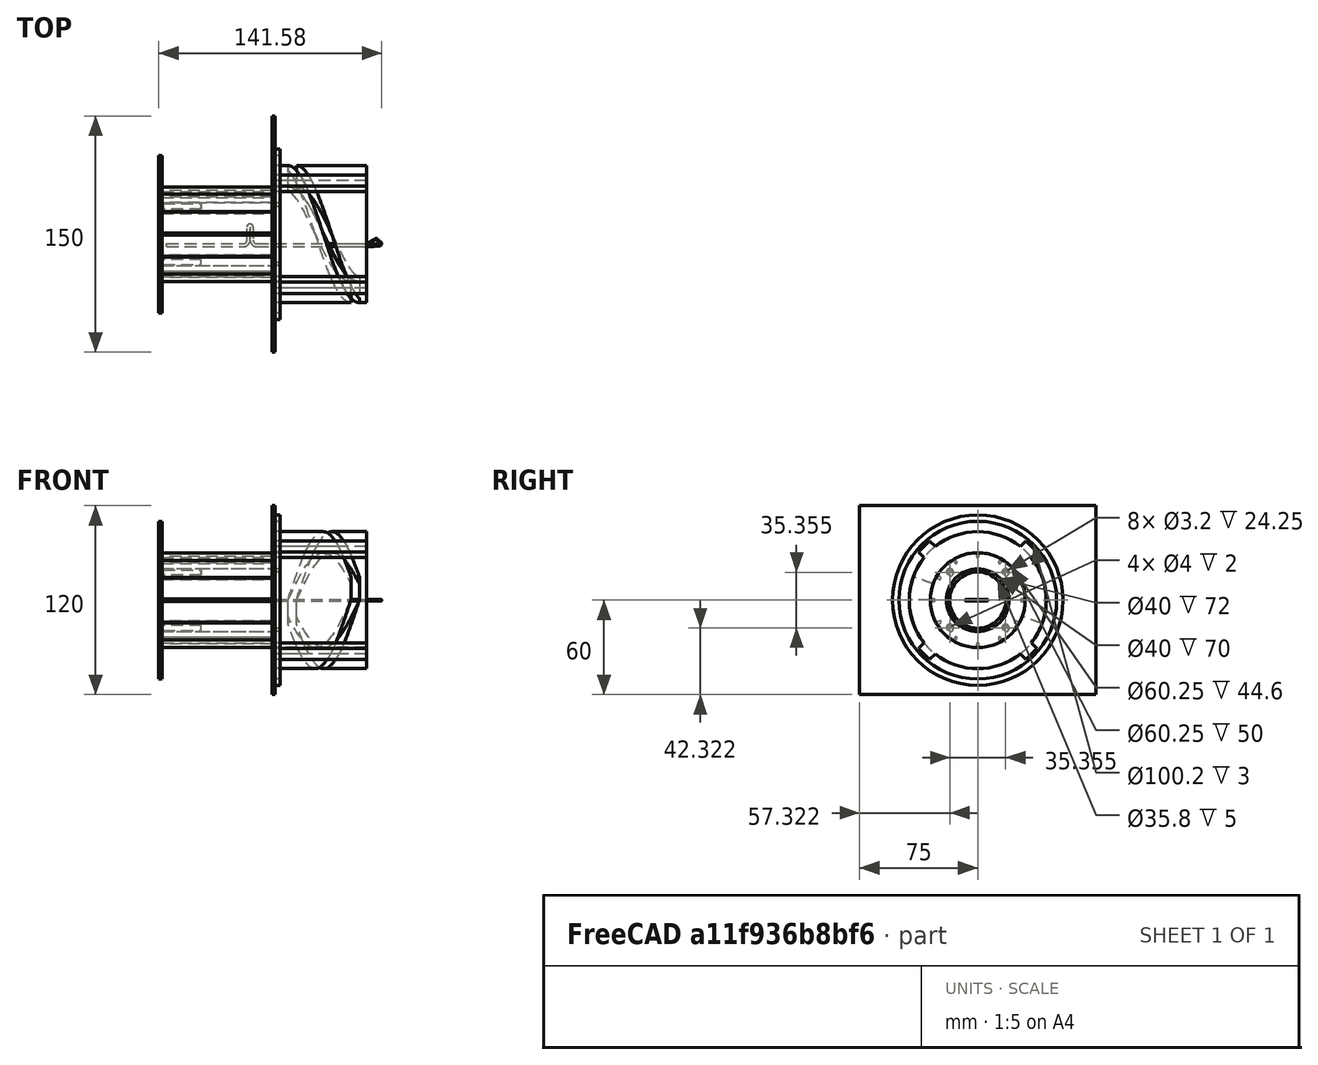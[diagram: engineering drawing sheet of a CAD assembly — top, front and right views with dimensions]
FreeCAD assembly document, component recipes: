
FREECAD ASSEMBLY — COMPONENT RECIPES ("knitting_machine")

This assembly document has 5 components, labeled P0..P4 below (a component is one placed body or linked part). 5 of them carry a construction recipe — the FreeCAD feature program that regenerates the part from scratch, quoted from this document or its linked companion documents; the rest are supplied as boundary geometry only. No exploded tour is included for this assembly.
COMPONENT P0 — recipe-attached ("Baseplate001", modeled in this document).
Construction recipe (the document's own serialized feature program — sketch geometry with constraints, then the solid features built on it; lengths are millimeters unless a unit is written):

FEATURE [Sketcher::SketchObject] Sketch012
  ArcFitTolerance = 1e-06
  AttachmentSupport = -> [YZ_Plane005]
  FullyConstrained = true
  MakeInternals = false
  MapMode = 5
  Placement = pos=(0,0,0) rot=(0.57735,0.57735,0.57735;2.0944rad)
  expr: Constraints[13] = <<MasterSpreadsheet>>.hole_diameter - 0.2 mm
  sketch-geometry (6):
    g0: LineSegment StartX=-75 StartY=60 StartZ=0 EndX=-75 EndY=-60 EndZ=0
    g1: LineSegment StartX=-75 StartY=-60 StartZ=0 EndX=75 EndY=-60 EndZ=0
    g2: LineSegment StartX=75 StartY=-60 StartZ=0 EndX=75 EndY=60 EndZ=0
    g3: LineSegment StartX=75 StartY=60 StartZ=0 EndX=-75 EndY=60 EndZ=0
    g4: GeomPoint [constr] X=0 Y=0 Z=0
    g5: Circle CenterX=0 CenterY=0 CenterZ=0 NormalX=0 NormalY=0 NormalZ=1 AngleXU=0 Radius=19.9
  constraints (14):
    c: Coincident(g0,g1)
    c: Coincident(g1,g2)
    c: Coincident(g2,g3)
    c: Coincident(g3,g0)
    c: Vertical(g0)
    c: Vertical(g2)
    c: Horizontal(g1)
    c: Horizontal(g3)
    c: Symmetric(g2,g0,g4)
    c: Coincident(g4,g-1)
    c: Coincident(g5,g4)
    c: DistanceX(g1,g1) = 150
    c: DistanceY(g0,g0) = 120
    c: Diameter(g5) = 39.8
FEATURE [PartDesign::Pad] Pad004
  Direction = (1,0,0)
  Length = 2
  Length2 = 10
  Placement = pos=(0,0,0) rot=(1,1,1;2.0944rad)
  Profile = -> Sketch012
  ReferenceAxis = -> Sketch012 [N_Axis]
  Refine = true
  Suppressed = false
  Type = 0
FEATURE [Sketcher::SketchObject] Sketch013
  ArcFitTolerance = 1e-06
  AttachmentSupport = -> [YZ_Plane005]
  ExternalGeometry = -> [Pad004]
  FullyConstrained = true
  MakeInternals = false
  MapMode = 5
  Placement = pos=(0,0,0) rot=(0.57735,0.57735,0.57735;2.0944rad)
  sketch-geometry (2):
    g0: Circle CenterX=0 CenterY=0 CenterZ=0 NormalX=0 NormalY=0 NormalZ=1 AngleXU=0 Radius=19.9
    g1: Circle CenterX=0 CenterY=0 CenterZ=0 NormalX=0 NormalY=0 NormalZ=1 AngleXU=0 Radius=17.9
  constraints (4):
    c: Coincident(g0,g-1)
    c: Equal(g-3,g0)
    c: Coincident(g1,g0)
    c: Distance(g1,g0) = 2
FEATURE [PartDesign::Pad] Pad005
  BaseFeature = -> Pad004
  Direction = (1,0,0)
  Length = 5
  Length2 = 10
  Offset = 1
  Placement = pos=(0,0,0) rot=(1,1,1;2.0944rad)
  Profile = -> Sketch013
  ReferenceAxis = -> Sketch013 [N_Axis]
  Refine = true
  Suppressed = false
  Type = 0
FEATURE [Sketcher::SketchObject] Sketch014
  ArcFitTolerance = 1e-06
  AttachmentSupport = -> [YZ_Plane005]
  FullyConstrained = true
  MakeInternals = false
  MapMode = 5
  Placement = pos=(0,0,0) rot=(0.57735,0.57735,0.57735;2.0944rad)
  sketch-geometry (2):
    g0: Circle CenterX=0 CenterY=0 CenterZ=0 NormalX=0 NormalY=0 NormalZ=1 AngleXU=0 Radius=50.1
    g1: Circle CenterX=0 CenterY=0 CenterZ=0 NormalX=0 NormalY=0 NormalZ=1 AngleXU=0 Radius=54.1
  constraints (4):
    c: Coincident(g0,g-1)
    c: Coincident(g1,g0)
    c: Diameter(g0) = 100.2
    c: Distance(g0,g1) = 4
FEATURE [PartDesign::Pad] Pad006
  BaseFeature = -> Pad005
  Direction = (1,0,0)
  Length = 10
  Length2 = 10
  Placement = pos=(0,0,0) rot=(1,1,1;2.0944rad)
  Profile = -> Sketch014
  ReferenceAxis = -> Sketch014 [N_Axis]
  Refine = true
  Suppressed = false
  Type = 3
  UpToFace = -> Pad005 [Face7]
FEATURE [PartDesign::Body] Body002  label="Body_baseplate"
  AllowCompound = false
  Group = -> [Sketch012,Pad004,Sketch013,Pad005,Sketch014,Pad006]
  Origin = -> Origin005
  Tip = -> Pad006
COMPONENT P1 — recipe-attached ("Needle001", modeled in this document).
Construction recipe (the document's own serialized feature program — sketch geometry with constraints, then the solid features built on it; lengths are millimeters unless a unit is written):

FEATURE [Sketcher::SketchObject] Sketch  label="Needle_profile"
  ArcFitTolerance = 1e-06
  AttachmentSupport = -> [XY_Plane001]
  FullyConstrained = true
  MakeInternals = false
  MapMode = 5
  expr: Constraints[19] = <<MasterSpreadsheet>>.needle_thickness + 0.1 mm
  expr: Constraints[29] = <<MasterSpreadsheet>>.needle_knob_protrusion
  sketch-geometry (11):
    g0: LineSegment StartX=-67 StartY=-7 StartZ=0 EndX=-18.2 EndY=-7 EndZ=0
    g1: LineSegment StartX=-15 StartY=-3.8 StartZ=0 EndX=-15 EndY=4.55 EndZ=0
    g2: LineSegment StartX=-13.95 StartY=5.5 StartZ=0 EndX=-14.05 EndY=5.5 EndZ=0
    g3: LineSegment StartX=-13 StartY=4.55 StartZ=0 EndX=-13 EndY=-3.8 EndZ=0
    g4: LineSegment StartX=-9.8 StartY=-7 StartZ=0 EndX=60 EndY=-7 EndZ=0
    g5: ArcOfCircle CenterX=-18.2 CenterY=-3.8 CenterZ=0 NormalX=0 NormalY=0 NormalZ=1 AngleXU=0 Radius=3.2 StartAngle=4.71239 EndAngle=6.28319
    g6: GeomPoint [constr] X=-15 Y=-7 Z=0
    g7: ArcOfCircle CenterX=-9.8 CenterY=-3.8 CenterZ=0 NormalX=0 NormalY=0 NormalZ=1 AngleXU=0 Radius=3.2 StartAngle=3.14159 EndAngle=4.71239
    g8: GeomPoint [constr] X=-13 Y=-7 Z=0
    g9: ArcOfCircle CenterX=-14.05 CenterY=4.55 CenterZ=0 NormalX=0 NormalY=0 NormalZ=1 AngleXU=0 Radius=0.95 StartAngle=1.5708 EndAngle=3.14159
    g10: ArcOfCircle CenterX=-13.95 CenterY=4.55 CenterZ=0 NormalX=0 NormalY=0 NormalZ=1 AngleXU=0 Radius=0.95 StartAngle=3e-16 EndAngle=1.5708
  constraints (30):
    c: Horizontal(g0)
    c: Vertical(g1)
    c: Vertical(g3)
    c: Horizontal(g4)
    c: Horizontal(g8,g6)
    c: Horizontal(g2)
    c: PointOnObject(g6,g0)
    c: PointOnObject(g6,g1)
    c: Tangent(g0,g5) = -1.5708
    c: Tangent(g1,g5) = -1.5708
    c: PointOnObject(g8,g3)
    c: PointOnObject(g8,g4)
    c: Tangent(g3,g7) = -1.5708
    c: Tangent(g4,g7) = -1.5708
    c: Equal(g5,g7)
    c: Distance(g0,g-1) = 7
    c: Distance(g0,g-2) = 67
    c: DistanceX(g-1,g4) = 60
    c: Distance(g3,g-2) = 13
    c: DistanceX(g1,g3) = 2
    c: Horizontal(g1,g3)
    c: Radius(g7) = 3.2
    c: Distance(g2,g2) = 0.1
    c: Coincident(g9,g1)
    c: Horizontal(g9,g1)
    c: Tangent(g9,g2) = -1.5708
    c: Coincident(g10,g3)
    c: Horizontal(g10,g3)
    c: Tangent(g10,g2) = -1.5708
    c: DistanceY(g4,g2) = 12.5
FEATURE [Sketcher::SketchObject] Sketch001  label="Needle_section"
  ArcFitTolerance = 1e-06
  AttachmentSupport = -> [YZ_Plane001]
  ExternalGeometry = -> [Sketch]
  FullyConstrained = true
  MakeInternals = false
  MapMode = 5
  Placement = pos=(0,0,0) rot=(0.57735,0.57735,0.57735;2.0944rad)
  expr: Constraints[26] = <<MasterSpreadsheet>>.needle_thickness
  expr: Constraints[27] = <<MasterSpreadsheet>>.needle_width
  sketch-geometry (13):
    g0: LineSegment StartX=-7.95 StartY=0.1 StartZ=0 EndX=-7.95 EndY=-0.1 EndZ=0
    g1: LineSegment StartX=-7.45 StartY=-0.6 StartZ=0 EndX=-6.55 EndY=-0.6 EndZ=0
    g2: LineSegment StartX=-6.05 StartY=-0.1 StartZ=0 EndX=-6.05 EndY=0.1 EndZ=0
    g3: LineSegment StartX=-6.55 StartY=0.6 StartZ=0 EndX=-7.45 EndY=0.6 EndZ=0
    g4: ArcOfCircle CenterX=-7.45 CenterY=0.1 CenterZ=0 NormalX=0 NormalY=0 NormalZ=1 AngleXU=0 Radius=0.5 StartAngle=1.5708 EndAngle=3.14159
    g5: ArcOfCircle CenterX=-7.45 CenterY=-0.1 CenterZ=0 NormalX=0 NormalY=0 NormalZ=1 AngleXU=0 Radius=0.5 StartAngle=3.14159 EndAngle=4.71239
    g6: ArcOfCircle CenterX=-6.55 CenterY=-0.1 CenterZ=0 NormalX=0 NormalY=0 NormalZ=1 AngleXU=0 Radius=0.5 StartAngle=4.71239 EndAngle=6.28319
    g7: ArcOfCircle CenterX=-6.55 CenterY=0.1 CenterZ=0 NormalX=0 NormalY=0 NormalZ=1 AngleXU=0 Radius=0.5 StartAngle=0 EndAngle=1.5708
    g8: GeomPoint [constr] X=-7.95 Y=0.6 Z=0
    g9: GeomPoint [constr] X=-6.05 Y=-0.6 Z=0
    g10: LineSegment [constr] StartX=-7.45 StartY=-0.1 StartZ=0 EndX=-6.55 EndY=0.1 EndZ=0
    g11: LineSegment [constr] StartX=-7.45 StartY=0.1 StartZ=0 EndX=-6.55 EndY=-0.1 EndZ=0
    g12: GeomPoint [constr] X=-7 Y=0 Z=0
  constraints (28):
    c: Tangent(g0,g4) = -1.5708
    c: Tangent(g0,g5) = -1.5708
    c: Tangent(g1,g5) = -1.5708
    c: Tangent(g1,g6) = -1.5708
    c: Tangent(g2,g6) = -1.5708
    c: Tangent(g2,g7) = -1.5708
    c: Tangent(g3,g7) = -1.5708
    c: Tangent(g3,g4) = -1.5708
    c: Vertical(g0)
    c: Vertical(g2)
    c: Horizontal(g1)
    c: Horizontal(g3)
    c: Equal(g4,g5)
    c: Equal(g5,g6)
    c: Equal(g6,g7)
    c: PointOnObject(g8,g0)
    c: PointOnObject(g8,g3)
    c: PointOnObject(g9,g1)
    c: PointOnObject(g9,g2)
    c: Radius(g5) = 0.5
    c: Coincident(g10,g5)
    c: Coincident(g10,g7)
    c: Coincident(g11,g4)
    c: Coincident(g11,g6)
    c: Symmetric(g10,g10,g12)
    c: Coincident(g12,g-3)
    c: DistanceX(g0,g2) = 1.9
    c: DistanceY(g1,g3) = 1.2
FEATURE [PartDesign::AdditivePipe] AdditivePipe
  AuxilleryCurvelinear = true
  AuxillerySpineTangent = false
  Binormal = (0,0,0)
  Mode = 0
  Placement = pos=(0,0,0) rot=(1,1,1;2.0944rad)
  Profile = -> Sketch001
  Refine = true
  Spine = -> Sketch
  SpineTangent = false
  Suppressed = false
  Transformation = 0
  Transition = 0
FEATURE [Sketcher::SketchObject] Sketch002
  ArcFitTolerance = 1e-06
  AttachmentSupport = -> [XY_Plane001]
  ExternalGeometry = -> [AdditivePipe]
  FullyConstrained = true
  MakeInternals = false
  MapMode = 5
  sketch-geometry (4):
    g0: GeomPoint X=60 Y=-7 Z=0
    g1: LineSegment StartX=60 StartY=-7 StartZ=0 EndX=68 EndY=-7 EndZ=0
    g2: ArcOfCircle CenterX=68 CenterY=-5.81584 CenterZ=0 NormalX=0 NormalY=0 NormalZ=1 AngleXU=0 Radius=1.18416 StartAngle=4.71239 EndAngle=7.73181
    g3: LineSegment StartX=68.1443 StartY=-4.6405 StartZ=0 EndX=67 EndY=-4.5 EndZ=0
  constraints (9):
    c: Symmetric(g-3,g-4,g0)
    c: Coincident(g1,g0)
    c: Horizontal(g1)
    c: Tangent(g2,g1) = -1.5708
    c: Tangent(g3,g2) = -1.5708
    c: DistanceX(g0,g3) = 7
    c: DistanceY(g0,g3) = 2.5
    c: Angle(g3,g-1) = 0.122173
    c: DistanceX(g0,g1) = 8
FEATURE [Sketcher::SketchObject] Sketch003
  ArcFitTolerance = 1e-06
  AttachmentSupport = -> [YZ_Plane001,Sketch002]
  ExternalGeometry = -> [Sketch002]
  FullyConstrained = true
  MakeInternals = false
  MapMode = 53
  Placement = pos=(68,-7.5e-15,7.5e-15) rot=(0.57735,0.57735,0.57735;2.0944rad)
  expr: Constraints[1] = <<MasterSpreadsheet>>.needle_width
  sketch-geometry (1):
    g0: Circle CenterX=-7 CenterY=0 CenterZ=0 NormalX=0 NormalY=0 NormalZ=1 AngleXU=0 Radius=0.6
  constraints (2):
    c: Coincident(g0,g-3)
    c: Diameter(g0) = 1.2
FEATURE [Sketcher::SketchObject] Sketch004
  ArcFitTolerance = 1e-06
  AttachmentSupport = -> [Sketch002]
  FullyConstrained = true
  MakeInternals = false
  MapMode = 1
  Placement = pos=(67,-4.5,0) rot=(0.624332,0.552363,0.552363;2.02535rad)
  sketch-geometry (1):
    g0: Circle CenterX=0 CenterY=0 CenterZ=0 NormalX=0 NormalY=0 NormalZ=1 AngleXU=0 Radius=0.15
  constraints (2):
    c: Diameter(g0) = 0.3
    c: Coincident(g0,g-1)
FEATURE [PartDesign::AdditiveLoft] AdditiveLoft
  BaseFeature = -> AdditivePipe
  Closed = false
  Placement = pos=(0,0,0) rot=(1,1,1;2.0944rad)
  Profile = -> AdditivePipe [Face49]
  Refine = true
  Ruled = false
  Sections = -> [Sketch003]
  Suppressed = false
FEATURE [Sketcher::SketchObject] Sketch005
  ArcFitTolerance = 1e-06
  AttachmentSupport = -> [Sketch002]
  FullyConstrained = true
  MakeInternals = false
  MapMode = 7
  Placement = pos=(68.1443,-4.6405,0) rot=(0.624332,0.552363,0.552363;2.02535rad)
  sketch-geometry (1):
    g0: Circle CenterX=0 CenterY=0 CenterZ=0 NormalX=0 NormalY=0 NormalZ=1 AngleXU=0 Radius=0.2
  constraints (2):
    c: Diameter(g0) = 0.4
    c: Coincident(g0,g-1)
FEATURE [PartDesign::AdditivePipe] AdditivePipe001
  AuxilleryCurvelinear = true
  AuxillerySpineTangent = false
  BaseFeature = -> AdditiveLoft
  Binormal = (0,0,0)
  Mode = 0
  Placement = pos=(0,0,0) rot=(1,1,1;2.0944rad)
  Profile = -> AdditiveLoft [Face55]
  Refine = true
  Sections = -> [Sketch005]
  Spine = -> Sketch002 [Edge2]
  SpineTangent = false
  Suppressed = false
  Transformation = 1
  Transition = 0
FEATURE [PartDesign::AdditiveLoft] AdditiveLoft001
  BaseFeature = -> AdditivePipe001
  Closed = false
  Placement = pos=(0,0,0) rot=(1,1,1;2.0944rad)
  Profile = -> AdditivePipe001 [Face68]
  Refine = true
  Ruled = false
  Sections = -> [Sketch004]
  Suppressed = false
FEATURE [Sketcher::SketchObject] Sketch006
  ArcFitTolerance = 1e-06
  AttachmentSupport = -> [AdditiveLoft001]
  ExternalGeometry = -> [AdditiveLoft001]
  FullyConstrained = true
  MakeInternals = false
  MapMode = 5
  Placement = pos=(0,-6.05,6.7e-15) rot=(0.57735,0.57735,0.57735;4.18879rad)
  sketch-geometry (5):
    g0: LineSegment StartX=-0.2 StartY=59.8 StartZ=0 EndX=0.2 EndY=59.8 EndZ=0
    g1: LineSegment StartX=0.2 StartY=59.8 StartZ=0 EndX=0.2 EndY=61.8 EndZ=0
    g2: LineSegment StartX=0.2 StartY=61.8 StartZ=0 EndX=-0.2 EndY=61.8 EndZ=0
    g3: LineSegment StartX=-0.2 StartY=61.8 StartZ=0 EndX=-0.2 EndY=59.8 EndZ=0
    g4: GeomPoint [constr] X=0 Y=60.8 Z=0
  constraints (13):
    c: Coincident(g0,g1)
    c: Coincident(g1,g2)
    c: Coincident(g2,g3)
    c: Coincident(g3,g0)
    c: Horizontal(g0)
    c: Horizontal(g2)
    c: Vertical(g1)
    c: Vertical(g3)
    c: Symmetric(g2,g0,g4)
    c: PointOnObject(g4,g-2)
    c: DistanceY(g1,g1) = 2
    c: Distance(g2,g2) = 0.4
    c: Distance(g-3,g0) = 0.2
FEATURE [PartDesign::Pad] Pad
  BaseFeature = -> AdditiveLoft001
  Direction = (-1e-16,1,-1e-15)
  Length = 0.3
  Length2 = 10
  Placement = pos=(0,0,0) rot=(1,1,1;2.0944rad)
  Profile = -> Sketch006
  ReferenceAxis = -> Sketch006 [N_Axis]
  Refine = true
  Reversed = true
  Suppressed = false
  Type = 0
FEATURE [Sketcher::SketchObject] Sketch007
  ArcFitTolerance = 1e-06
  AttachmentSupport = -> [Pad]
  ExternalGeometry = -> [Pad]
  FullyConstrained = true
  MakeInternals = false
  MapMode = 5
  Placement = pos=(-1e-16,3e-16,0.2) rot=(0,0,-1;1.5708rad)
  sketch-geometry (6):
    g0: LineSegment StartX=6.05 StartY=59.8 StartZ=0 EndX=3.01351 EndY=65.3199 EndZ=0
    g1: LineSegment StartX=6.05 StartY=59.8 StartZ=0 EndX=6.05 EndY=61.8 EndZ=0
    g2: LineSegment StartX=6.05 StartY=61.8 StartZ=0 EndX=3.18212 EndY=65.8958 EndZ=0
    g3: ArcOfCircle CenterX=4.76587 CenterY=66.2839 CenterZ=0 NormalX=0 NormalY=0 NormalZ=1 AngleXU=0 Radius=2 StartAngle=2.9064 EndAngle=3.64451
    g4: ArcOfCircle CenterX=3.01542 CenterY=66.7034 CenterZ=0 NormalX=0 NormalY=0 NormalZ=1 AngleXU=0 Radius=0.2 StartAngle=6.24175 EndAngle=9.18959
    g5: LineSegment StartX=3.18212 StartY=65.8958 StartZ=0 EndX=3.21525 EndY=66.6951 EndZ=0
  constraints (15):
    c: Coincident(g-3,g0)
    c: Coincident(g0,g1)
    c: Coincident(g1,g-3)
    c: Coincident(g1,g2)
    c: Coincident(g5,g2)
    c: Tangent(g5,g4) = -1.5708
    c: Tangent(g3,g0) = 1.5708
    c: Tangent(g4,g3) = -1.5708
    c: Radius(g4) = 0.2
    c: Radius(g3) = 2
    c: Distance(g0,g2) = 0.6
    c: Distance(g2,g2) = 5
    c: Distance(g0,g0) = 6.3
    c: Distance(g5,g5) = 0.8
    c: Angle(g-2,g2) = 0.610865
FEATURE [PartDesign::Pad] Pad001
  BaseFeature = -> Pad
  Direction = (0,1.3e-15,1)
  Length = 10
  Length2 = 10
  Placement = pos=(0,0,0) rot=(1,1,1;2.0944rad)
  Profile = -> Sketch007
  ReferenceAxis = -> Sketch007 [N_Axis]
  Refine = true
  Reversed = true
  Suppressed = false
  Type = 3
  UpToFace = -> Pad [Face54]
FEATURE [PartDesign::Body] Body  label="Body_needle"
  AllowCompound = false
  Group = -> [Sketch,Sketch001,AdditivePipe,Sketch002,Sketch003,Sketch004,AdditiveLoft,Sketch005,AdditivePipe001,AdditiveLoft001,Sketch006,Pad,Sketch007,Pad001]
  Origin = -> Origin001
  Tip = -> Pad001
COMPONENT P2 — same part as P1; its construction recipe is shown at P1.
COMPONENT P3 — recipe-attached ("Needle_guide001", modeled in this document).
Construction recipe (the document's own serialized feature program — sketch geometry with constraints, then the solid features built on it; lengths are millimeters unless a unit is written):

FEATURE [Sketcher::SketchObject] Sketch008
  ArcFitTolerance = 1e-06
  AttachmentSupport = -> [YZ_Plane003]
  FullyConstrained = true
  MakeInternals = false
  MapMode = 5
  Placement = pos=(0,0,0) rot=(0.57735,0.57735,0.57735;2.0944rad)
  expr: Constraints[2] = <<MasterSpreadsheet>>.hole_diameter
  sketch-geometry (2):
    g0: Circle CenterX=0 CenterY=0 CenterZ=0 NormalX=0 NormalY=0 NormalZ=1 AngleXU=0 Radius=20
    g1: Circle CenterX=0 CenterY=0 CenterZ=0 NormalX=0 NormalY=0 NormalZ=1 AngleXU=0 Radius=30
  constraints (4):
    c: Coincident(g0,g-1)
    c: Coincident(g1,g0)
    c: Diameter(g0) = 40
    c: Distance(g1,g0) = 10
FEATURE [PartDesign::Pad] Pad002
  Direction = (1,0,0)
  Length = 70
  Length2 = 10
  Placement = pos=(0,0,0) rot=(1,1,1;2.0944rad)
  Profile = -> Sketch008
  ReferenceAxis = -> Sketch008 [N_Axis]
  Refine = true
  Reversed = true
  Suppressed = false
  Type = 0
FEATURE [Sketcher::SketchObject] Sketch009
  ArcFitTolerance = 1e-06
  AttachmentSupport = -> [Pad002]
  ExternalGeometry = -> [Pad002]
  FullyConstrained = true
  MakeInternals = false
  MapMode = 5
  Placement = pos=(0,0,0) rot=(0.57735,0.57735,0.57735;2.0944rad)
  expr: Constraints[17] = <<MasterSpreadsheet>>.needle_thickness
  expr: Constraints[18] = <<MasterSpreadsheet>>.needle_width + 0.2 mm
  sketch-geometry (8):
    g0: ArcOfCircle CenterX=29.573 CenterY=1.26471 CenterZ=0 NormalX=0 NormalY=0 NormalZ=1 AngleXU=0 Radius=0.4 StartAngle=4.79966 EndAngle=6.32592
    g1: ArcOfCircle CenterX=27.7078 CenterY=0 CenterZ=0 NormalX=0 NormalY=0 NormalZ=1 AngleXU=0 Radius=0.7 StartAngle=1.5708 EndAngle=4.71239
    g2: ArcOfCircle CenterX=29.573 CenterY=-1.26471 CenterZ=0 NormalX=0 NormalY=0 NormalZ=1 AngleXU=0 Radius=0.4 StartAngle=6.24045 EndAngle=7.76672
    g3: ArcOfCircle CenterX=0 CenterY=0 CenterZ=0 NormalX=0 NormalY=0 NormalZ=1 AngleXU=0 Radius=30 StartAngle=6.24045 EndAngle=6.32592
    g4: LineSegment StartX=27.7078 StartY=0.7 StartZ=0 EndX=29.6078 EndY=0.866228 EndZ=0
    g5: LineSegment StartX=29.6078 StartY=-0.866228 StartZ=0 EndX=27.7078 EndY=-0.7 EndZ=0
    g6: LineSegment [constr] StartX=29.6078 StartY=0.866228 StartZ=0 EndX=29.6078 EndY=-0.866228 EndZ=0
    g7: GeomPoint [constr] X=29.6078 Y=0 Z=0
  constraints (21):
    c: PointOnObject(g0,g-3)
    c: PointOnObject(g1,g-1)
    c: Equal(g2,g0)
    c: Coincident(g3,g-1)
    c: Coincident(g5,g1)
    c: Tangent(g3,g2) = -1.5708
    c: Tangent(g3,g0) = -1.5708
    c: Coincident(g4,g1)
    c: Vertical(g1,g1)
    c: Vertical(g1,g1)
    c: Coincident(g0,g4)
    c: Coincident(g6,g0)
    c: Coincident(g6,g2)
    c: Vertical(g6)
    c: Symmetric(g6,g6,g7)
    c: PointOnObject(g7,g-1)
    c: Radius(g0) = 0.4
    c: DistanceX(g1,g7) = 1.9
    c: DistanceY(g1,g1) = 1.4
    c: Angle(g-1,g4) = 0.0872665
    c: Tangent(g5,g2) = -1.5708
FEATURE [PartDesign::Pocket] Pocket
  BaseFeature = -> Pad002
  Direction = (-1,0,0)
  Length = 5
  Length2 = 5
  Placement = pos=(0,0,0) rot=(1,1,1;2.0944rad)
  Profile = -> Sketch009
  ReferenceAxis = -> Sketch009 [N_Axis]
  Refine = true
  Suppressed = false
  Type = 2
FEATURE [PartDesign::PolarPattern] PolarPattern
  Angle = 360
  Axis = -> Sketch009 [N_Axis]
  BaseFeature = -> Pocket
  Mode = 0
  Occurrences = 12
  Offset = 120
  Originals = -> [Pocket]
  Placement = pos=(0,0,0) rot=(1,1,1;2.0944rad)
  Refine = true
  Suppressed = false
  TransformMode = 0
  expr: Occurrences = <<MasterSpreadsheet>>.needle_number
FEATURE [Sketcher::SketchObject] Sketch019
  ArcFitTolerance = 1e-06
  AttachmentSupport = -> [PolarPattern]
  ExternalGeometry = -> [PolarPattern]
  FullyConstrained = true
  MakeInternals = false
  MapMode = 5
  Placement = pos=(-70,3.11e-14,-1.55e-14) rot=(0.57735,0.57735,-0.57735;4.18879rad)
  sketch-geometry (2):
    g0: Circle CenterX=17.6777 CenterY=-17.6777 CenterZ=0 NormalX=0 NormalY=0 NormalZ=1 AngleXU=0 Radius=1.6
    g1: LineSegment [constr] StartX=0 StartY=0 StartZ=0 EndX=17.6777 EndY=-17.6777 EndZ=0
  constraints (5):
    c: Coincident(g1,g-1)
    c: Coincident(g1,g0)
    c: Angle(g1,g-1) = 0.785398
    c: Diameter(g0) = 3.2
    c: Distance(g0,g-3) = 5
FEATURE [PartDesign::Pocket] Pocket001
  BaseFeature = -> PolarPattern
  Direction = (1,0,0)
  Length = 25
  Length2 = 5
  Placement = pos=(0,0,0) rot=(1,1,1;2.0944rad)
  Profile = -> Sketch019
  ReferenceAxis = -> Sketch019 [N_Axis]
  Refine = true
  Suppressed = false
  Type = 0
FEATURE [PartDesign::PolarPattern] PolarPattern002
  Angle = 360
  Axis = -> Sketch019 [N_Axis]
  BaseFeature = -> Pocket001
  Mode = 0
  Occurrences = 4
  Offset = 120
  Originals = -> [Pocket001]
  Placement = pos=(0,0,0) rot=(1,1,1;2.0944rad)
  Refine = true
  Suppressed = false
  TransformMode = 0
FEATURE [PartDesign::Chamfer] Chamfer
  Angle = 45
  Base = -> PolarPattern002 [Edge149,Edge151,Edge153,Edge150]
  BaseFeature = -> PolarPattern002
  ChamferType = 0
  FlipDirection = false
  Placement = pos=(0,0,0) rot=(1,1,1;2.0944rad)
  Refine = true
  Size = 0.75
  Size2 = 1
  SupportTransform = false
  Suppressed = false
  UseAllEdges = false
FEATURE [PartDesign::Body] Body001  label="needleguide001"
  AllowCompound = false
  Group = -> [Sketch008,Pad002,Sketch009,Pocket,PolarPattern,Sketch019,Pocket001,PolarPattern002,Chamfer]
  Origin = -> Origin003
  Tip = -> Chamfer
FEATURE [Sketcher::SketchObject] Sketch020
  ArcFitTolerance = 1e-06
  AttachmentSupport = -> [Chamfer]
  FullyConstrained = true
  MakeInternals = false
  MapMode = 5
  Placement = pos=(-70,4.66e-14,-2.33e-14) rot=(0.57735,0.57735,-0.57735;4.18879rad)
  expr: Constraints[2] = <<MasterSpreadsheet>>.hole_diameter
  expr: Constraints[3] = <<MasterSpreadsheet>>.baseplate_diameter
  sketch-geometry (10):
    g0: Circle CenterX=0 CenterY=0 CenterZ=0 NormalX=0 NormalY=0 NormalZ=1 AngleXU=0 Radius=20
    g1: Circle CenterX=0 CenterY=0 CenterZ=0 NormalX=0 NormalY=0 NormalZ=1 AngleXU=0 Radius=50
    g2: Circle CenterX=17.6777 CenterY=17.6777 CenterZ=0 NormalX=0 NormalY=0 NormalZ=1 AngleXU=0 Radius=2
    g3: LineSegment [constr] StartX=0 StartY=0 StartZ=0 EndX=17.6777 EndY=17.6777 EndZ=0
    g4: Circle CenterX=-17.6777 CenterY=17.6777 CenterZ=0 NormalX=0 NormalY=0 NormalZ=1 AngleXU=0 Radius=2
    g5: LineSegment [constr] StartX=0 StartY=0 StartZ=0 EndX=-17.6777 EndY=17.6777 EndZ=0
    g6: Circle CenterX=-17.6777 CenterY=-17.6777 CenterZ=0 NormalX=0 NormalY=0 NormalZ=1 AngleXU=0 Radius=2
    g7: LineSegment [constr] StartX=0 StartY=0 StartZ=0 EndX=-17.6777 EndY=-17.6777 EndZ=0
    g8: Circle CenterX=17.6777 CenterY=-17.6777 CenterZ=0 NormalX=0 NormalY=0 NormalZ=1 AngleXU=0 Radius=2
    g9: LineSegment [constr] StartX=0 StartY=0 StartZ=0 EndX=17.6777 EndY=-17.6777 EndZ=0
  constraints (24):
    c: Coincident(g0,g-1)
    c: Coincident(g1,g0)
    c: Diameter(g0) = 40
    c: Diameter(g1) = 100
    c: Diameter(g2) = 4
    c: Coincident(g3,g0)
    c: Coincident(g3,g2)
    c: Angle(g-1,g3) = 0.785398
    c: Distance(g2,g0) = 5
    c: Diameter(g4) = 4
    c: Diameter(g6) = 4
    c: Diameter(g8) = 4
    c: Coincident(g5,g4)
    c: Coincident(g7,g6)
    c: Coincident(g9,g8)
    c: Equal(g9,g3)
    c: Equal(g3,g5)
    c: Equal(g5,g7)
    c: Coincident(g5,g9)
    c: Coincident(g5,g7)
    c: Coincident(g5,g0)
    c: Perpendicular(g5,g3)
    c: Perpendicular(g5,g7)
    c: Perpendicular(g7,g9)
FEATURE [PartDesign::Pad] Pad009
  Direction = (-1,0,0)
  Length = 2
  Length2 = 10
  Placement = pos=(0,0,0) rot=(1,1,1;2.0944rad)
  Profile = -> Sketch020
  ReferenceAxis = -> Sketch020 [N_Axis]
  Refine = true
  Suppressed = false
  Type = 0
FEATURE [PartDesign::Body] Body004  label="needleGuide_baseplate"
  AllowCompound = false
  Group = -> [Sketch020,Pad009]
  Origin = -> Origin009
  Tip = -> Pad009
COMPONENT P4 — recipe-attached ("track001", modeled in this document).
Construction recipe (the document's own serialized feature program — sketch geometry with constraints, then the solid features built on it; lengths are millimeters unless a unit is written):

FEATURE [Sketcher::SketchObject] Sketch015
  ArcFitTolerance = 1e-06
  AttachmentSupport = -> [YZ_Plane008]
  FullyConstrained = true
  MakeInternals = false
  MapMode = 5
  Placement = pos=(0,0,0) rot=(0.57735,0.57735,0.57735;2.0944rad)
  expr: Constraints[3] = 60 mm + 2 mm + 2 * <<MasterSpreadsheet>>.needle_knob_protrusion
  sketch-geometry (2):
    g0: Circle CenterX=0 CenterY=0 CenterZ=0 NormalX=0 NormalY=0 NormalZ=1 AngleXU=0 Radius=30.125
    g1: Circle CenterX=0 CenterY=0 CenterZ=0 NormalX=0 NormalY=0 NormalZ=1 AngleXU=0 Radius=43.5
  constraints (4):
    c: Coincident(g0,g-1)
    c: Coincident(g1,g0)
    c: Diameter(g0) = 60.25
    c: Diameter(g1) = 87
FEATURE [PartDesign::Pad] Pad007
  Direction = (1,0,0)
  Length = 60
  Length2 = 10
  Placement = pos=(0,0,0) rot=(1,1,1;2.0944rad)
  Profile = -> Sketch015
  ReferenceAxis = -> Sketch015 [N_Axis]
  Refine = true
  Suppressed = false
  Type = 0
  expr: Length = <<MasterSpreadsheet>>.travel_dist + 20 mm
FEATURE [Sketcher::SketchObject] Sketch017
  ArcFitTolerance = 1e-06
  AttachmentSupport = -> [Pad007]
  ExternalGeometry = -> [Pad007]
  FullyConstrained = true
  MakeInternals = false
  MapMode = 5
  Placement = pos=(60,-1.33e-14,6.7e-15) rot=(0.57735,0.57735,0.57735;2.0944rad)
  sketch-geometry (6):
    g0: LineSegment StartX=-34.0908 StartY=27.0197 StartZ=0 EndX=-27.0197 EndY=34.0908 EndZ=0
    g1: LineSegment StartX=-34.0908 StartY=27.0197 StartZ=0 EndX=-37.6263 EndY=30.5553 EndZ=0
    g2: LineSegment StartX=-37.6263 StartY=30.5553 StartZ=0 EndX=-30.5553 EndY=37.6263 EndZ=0
    g3: LineSegment StartX=-30.5553 StartY=37.6263 StartZ=0 EndX=-27.0197 EndY=34.0908 EndZ=0
    g4: GeomPoint X=-30.5553 Y=30.5553 Z=0
    g5: LineSegment [constr] StartX=0 StartY=0 StartZ=0 EndX=-30.5553 EndY=30.5553 EndZ=0
  constraints (15):
    c: PointOnObject(g0,g-3)
    c: PointOnObject(g0,g-3)
    c: Coincident(g0,g1)
    c: Coincident(g1,g2)
    c: Coincident(g2,g3)
    c: Coincident(g3,g0)
    c: Perpendicular(g2,g3)
    c: Perpendicular(g2,g1)
    c: Perpendicular(g0,g1)
    c: Distance(g1,g1) = 5
    c: Distance(g2,g2) = 10
    c: Symmetric(g0,g0,g4)
    c: Coincident(g5,g-1)
    c: Coincident(g5,g4)
    c: Angle(g-2,g5) = 0.785398
FEATURE [PartDesign::Pad] Pad008
  BaseFeature = -> Pad007
  Direction = (1,0,0)
  Length = 8
  Length2 = 10
  Placement = pos=(0,0,0) rot=(1,1,1;2.0944rad)
  Profile = -> Sketch017
  ReferenceAxis = -> Sketch017 [N_Axis]
  Refine = true
  Reversed = true
  Suppressed = false
  Type = 3
  UpToFace = -> Pad007 [Face3]
FEATURE [PartDesign::PolarPattern] PolarPattern001
  Angle = 360
  Axis = -> Sketch015 [N_Axis]
  BaseFeature = -> Pad008
  Mode = 0
  Occurrences = 4
  Offset = 120
  Originals = -> [Pad008]
  Placement = pos=(0,0,0) rot=(1,1,1;2.0944rad)
  Refine = true
  Suppressed = false
  TransformMode = 0
FEATURE [Sketcher::SketchObject] Sketch018
  ArcFitTolerance = 1e-06
  AttachmentSupport = -> [XY_Plane008]
  ExternalGeometry = -> [PolarPattern001]
  FullyConstrained = true
  MakeInternals = false
  MapMode = 5
  expr: Constraints[14] = <<MasterSpreadsheet>>.needle_knob_height + 1.5 mm
  sketch-geometry (6):
    g0: LineSegment [constr] StartX=0 StartY=43.5 StartZ=0 EndX=60 EndY=43.5 EndZ=0
    g1: LineSegment [constr] StartX=60 StartY=30.125 StartZ=0 EndX=0 EndY=30.125 EndZ=0
    g2: LineSegment StartX=10 StartY=43.5 StartZ=0 EndX=10 EndY=30.125 EndZ=0
    g3: LineSegment StartX=10 StartY=30.125 StartZ=0 EndX=15.4 EndY=30.125 EndZ=0
    g4: LineSegment StartX=15.4 StartY=30.125 StartZ=0 EndX=15.4 EndY=43.5 EndZ=0
    g5: LineSegment StartX=15.4 StartY=43.5 StartZ=0 EndX=10 EndY=43.5 EndZ=0
  constraints (16):
    c: Coincident(g0,g-4)
    c: Coincident(g0,g-6)
    c: Coincident(g1,g-5)
    c: Coincident(g1,g-3)
    c: Coincident(g2,g3)
    c: Coincident(g3,g4)
    c: Coincident(g4,g5)
    c: Coincident(g5,g2)
    c: Vertical(g2)
    c: Vertical(g4)
    c: Horizontal(g3)
    c: Horizontal(g5)
    c: PointOnObject(g2,g0)
    c: PointOnObject(g3,g1)
    c: DistanceX(g5,g5) = 5.4
    c: DistanceX(g0,g2) = 10
FEATURE [PartDesign::SubtractiveHelix] SubtractiveHelix
  Angle = 0
  Axis = (1,0,0)
  Base = (0,0,0)
  BaseFeature = -> PolarPattern001
  Growth = 0
  HasBeenEdited = true
  Height = 40
  LeftHanded = false
  Mode = 2
  Outside = false
  Pitch = 90
  Placement = pos=(0,0,0) rot=(1,1,1;2.0944rad)
  Profile = -> Sketch018
  ReferenceAxis = -> X_Axis008
  Refine = true
  Suppressed = false
  Tolerance = 0.1
  Turns = 0.444444
  expr: Height = <<MasterSpreadsheet>>.travel_dist
  expr: Turns = <<MasterSpreadsheet>>.travel_angle / 360 °
FEATURE [PartDesign::Groove] Groove
  Angle = 20
  Angle2 = 60
  Axis = (1,0,0)
  Base = (0,0,0)
  BaseFeature = -> SubtractiveHelix
  Placement = pos=(0,0,0) rot=(1,1,1;2.0944rad)
  Profile = -> SubtractiveHelix [Face22]
  ReferenceAxis = -> X_Axis008
  Refine = true
  Suppressed = false
  Type = 0
  expr: Angle = 180 ° - <<MasterSpreadsheet>>.travel_angle
FEATURE [PartDesign::SubtractiveHelix] SubtractiveHelix001
  Angle = 0
  Axis = (1,0,0)
  Base = (0,0,0)
  BaseFeature = -> Groove
  Growth = 0
  HasBeenEdited = true
  Height = 40
  LeftHanded = true
  Mode = 2
  Outside = false
  Pitch = 90
  Placement = pos=(0,0,0) rot=(1,1,1;2.0944rad)
  Profile = -> Groove [Face23]
  ReferenceAxis = -> X_Axis008
  Refine = true
  Reversed = true
  Suppressed = false
  Tolerance = 0.1
  Turns = 0.444444
  expr: Height = <<MasterSpreadsheet>>.travel_dist
  expr: Turns = <<MasterSpreadsheet>>.travel_angle / 360 °
FEATURE [PartDesign::Groove] Groove001
  Angle = 20
  Angle2 = 60
  Axis = (1,0,0)
  Base = (0,0,0)
  BaseFeature = -> SubtractiveHelix001
  Placement = pos=(0,0,0) rot=(1,1,1;2.0944rad)
  Profile = -> SubtractiveHelix001 [Face15]
  ReferenceAxis = -> X_Axis008
  Refine = true
  Suppressed = false
  Type = 0
  expr: Angle = 180 ° - <<MasterSpreadsheet>>.travel_angle
FEATURE [PartDesign::Body] Body003  label="BotTrack"
  AllowCompound = false
  Group = -> [Sketch015,Pad007,Sketch017,Pad008,PolarPattern001,Sketch018,SubtractiveHelix,Groove,SubtractiveHelix001,Groove001]
  Origin = -> Origin008
  Tip = -> Groove001
PROVENANCE & LICENSES
A FreeCAD (.FCStd) document from a public repository crawl; recipes are the document's own serialized feature recipes (and, for linked parts, companion documents' recipes).
License: mit.
